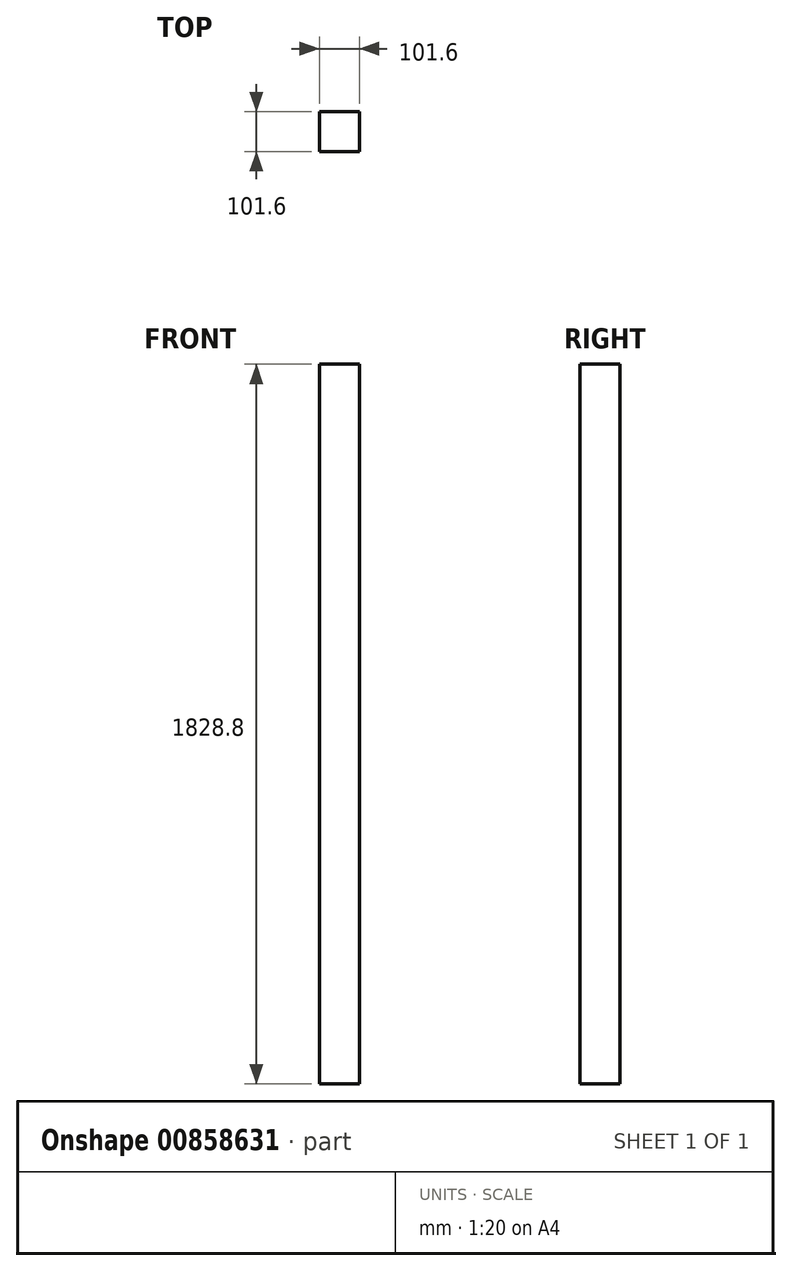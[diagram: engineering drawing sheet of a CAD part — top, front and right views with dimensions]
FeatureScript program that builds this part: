
annotation { "Feature Type Name" : "Feature", "Feature Type Description" : "" }
export const myFeature = defineFeature(function(context is Context, id is Id, definition is map)
    precondition{}
    {
        {
            var Q0;
            Q0=qCreatedBy(makeId("Top.planeOp"),FACE);
            var sketch = newSketch(context, id + "F0", { "sketchPlane" : qUnion([Q0])});
            skLineSegment(sketch, "E0.bottom", {"start": v(50.8, 50.8) * mm, "end": v(-50.8, 50.8) * mm});
            skLineSegment(sketch, "E0.top", {"start": v(50.8, -50.8) * mm, "end": v(-50.8, -50.8) * mm});
            skLineSegment(sketch, "E0.left", {"start": v(50.8, 50.8) * mm, "end": v(50.8, -50.8) * mm});
            skLineSegment(sketch, "E0.right", {"start": v(-50.8, 50.8) * mm, "end": v(-50.8, -50.8) * mm});
            skPoint(sketch, "E0.middle", {"position": v(0, 0) * mm});
            skSolve(sketch);
        }
        {
            var Q0;
            Q0 = qSketchRegion(id + "F0", true);
            extrude(context, id + "F1", {"entities" : qUnion([Q0]), "depth" : 1828.8 * mm, "offsetDistance" : 25.4 * mm});
        }
    });
